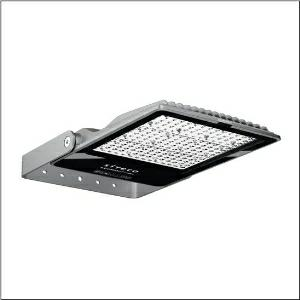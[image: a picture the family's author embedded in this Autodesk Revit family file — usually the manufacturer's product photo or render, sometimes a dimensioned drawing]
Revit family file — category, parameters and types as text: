
# Revit family: sicompact_r__31_midi___pl32_5xa7581d1k23_6975
name_source: partatom
category: Lighting Fixtures
units: mm (PartAtom-declared; Revit-internal decimal feet)

## family parameters
Cut with Voids When Loaded = No
Host = Face
Light Source = No
Part Type = Normal
Room Calculation Point = No
Round Connector Dimension = Use Diameter
Shared = No

## types (1)
- SiCompact® 31 midi  PL32 (1 x LED, 27000 lm, 171 W, 3000K)
    Apparent Load = 171 VA
    CIE Flux Codes = 32 69 98 100 100
    Color Rendering = 70
    Color Temperature = 3000K
    Default Elevation = 1800 mm
    Description = SiCompact® 31 midi, floodlight, primary light control with lens, of plastic, of toughened safety glass, transparent, light distribution: PL32, light emission: direct distribution, primary light characteristic: asymmetric, installation type: surface-mounted, LED, High Power LED, rated luminous flux: 27.000lm, luminous efficacy: 158lm/W, light colour: 730, colour temperature: 3000K, control gear: ON/OFF, with cable, 3x 1.5mm², mains connection: 220..240V, AC, 50/60Hz, connection cable pre-assembled, cable length: 2m, rated input power: 171W, of diecast aluminium, specular, metallic grey (RAL 9006), length: 560mm, width: 330mm, height: 62mm, bracket, of sheet steel, coated, metallic grey (RAL 9006), ON/OFF, protection rating (complete): IP66, insulation class (complete): insulation class I (protective earthing), certification: CE, ENEC, impact resistance: IK08, permissible operating ambient temperature: -40..+45°C, packaging unit: 1 piece

Light Distribution: PL32
    Height = 62 mm  [stored 0.203412 ft]
    Lamp = 1 x LED
    Lamp Light Flux = 27000 lm
    Lamp Power = 171 W
    Lamp count = 1
    Length = 560 mm
    Luminous efficacy = 158 lm/W
    Manufacturer = Siteco
    ModVariant = No
    Model = 5XA7581D1K23
    Mounting Place = Wall
    Mounting Type = Surface mounted
    Number of Poles = 1
    OnlyDefault = Yes
    Power Factor = 1
    Product Name = SiCompact® 31 midi | PL32
    Product group = floodlight | wall mounted
    ProductGroupID = 2001
    Protection Class = Protection class I
    Protection Degree = IP 66
    RLX_Detail_Level = 1
    RLX_Emergency_Light_Flux = 0 lm
    RLX_Emergency_Type = 0
    RLX_Emergency_Type_DB = No
    RlxData = <blob elided: 98145 chars, md5=37669f71>
    Socket = socket
    Standby Power = 0 W
    System Light Flux = 27000 lm
    System Power = 171 W
    Type Comments = Product without accessories
    Type Image = l_1006415.jpg
    URL = http://relux.com
    VarID = ---
    Voltage = 0 V
    Weight = 0.00 kg
    Width = 333 mm

note: [stored X ft] marks values corroborated as IEEE doubles in the binary element streams (Revit-internal decimal feet)

## geometry (parser evidence)
native form markers: Blend x4, Sweep x11
no freeform markers — native parametric forms only
